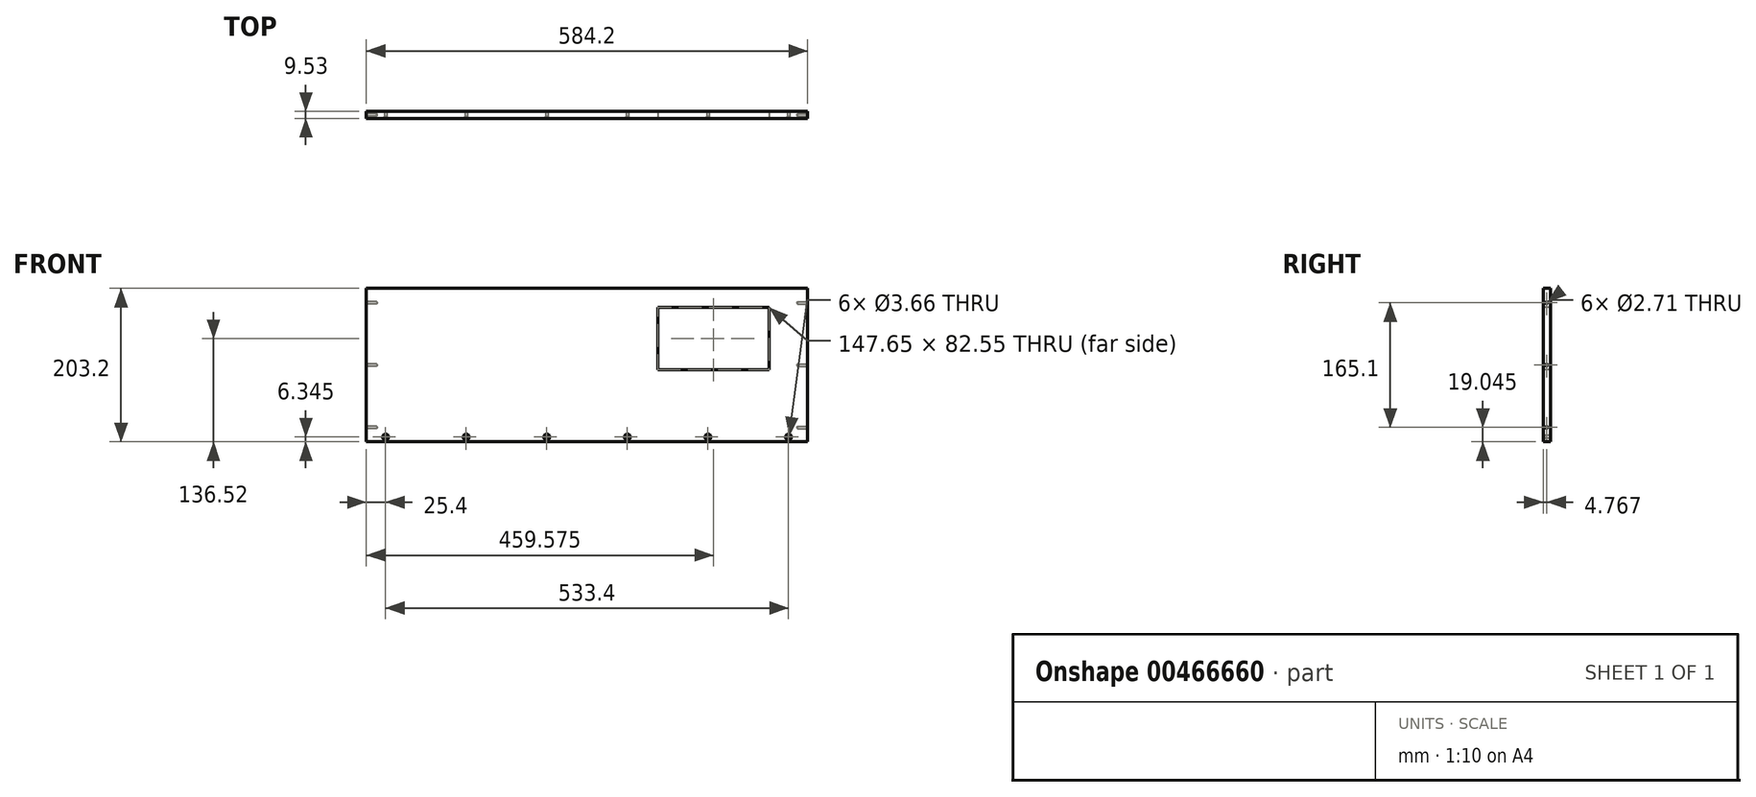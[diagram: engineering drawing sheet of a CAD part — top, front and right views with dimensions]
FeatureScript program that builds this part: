
annotation { "Feature Type Name" : "Feature", "Feature Type Description" : "" }
export const myFeature = defineFeature(function(context is Context, id is Id, definition is map)
    precondition{}
    {
        {
            var Q0;
            Q0=qCreatedBy(makeId("Front.planeOp"),FACE);
            var sketch = newSketch(context, id + "F0", { "sketchPlane" : qUnion([Q0])});
            skLineSegment(sketch, "E0.bottom", {"start": v(0, -14.34) * mm, "end": v(-584.2, -14.34) * mm});
            skLineSegment(sketch, "E0.top", {"start": v(0, 188.86) * mm, "end": v(-584.2, 188.86) * mm});
            skLineSegment(sketch, "E0.left", {"start": v(0, -14.34) * mm, "end": v(0, 188.86) * mm});
            skLineSegment(sketch, "E0.right", {"start": v(-584.2, -14.34) * mm, "end": v(-584.2, 188.86) * mm});
            skSolve(sketch);
        }
        {
            var Q0;
            Q0 = qSketchRegion(id + "F0", true);
            extrude(context, id + "F1", {"entities" : qUnion([Q0]), "depth" : 9.52 * mm});
        }
        {
            var Q0;
            Q0=makeQuery(id+"F1.opExtrude","CAP_FACE",FACE,{"disambiguationData":[OSD([sQuery(id+"F0.wireOp",EDGE,"E0.bottom"),sQuery(id+"F0.wireOp",EDGE,"E0.top"),sQuery(id+"F0.wireOp",EDGE,"E0.left"),sQuery(id+"F0.wireOp",EDGE,"E0.right")])],"isStart":false});
            var sketch = newSketch(context, id + "F2", { "sketchPlane" : qUnion([Q0])});
            skPoint(sketch, "E1", {"position": v(-25.4, -8) * mm});
            skPoint(sketch, "E2.1.0.0", {"position": v(-132.08, -8) * mm});
            skPoint(sketch, "E2.2.0.0", {"position": v(-238.76, -8) * mm});
            skPoint(sketch, "E2.3.0.0", {"position": v(-345.44, -8) * mm});
            skPoint(sketch, "E2.4.0.0", {"position": v(-452.12, -8) * mm});
            skPoint(sketch, "E2.5.0.0", {"position": v(-558.8, -8) * mm});
            skLineSegment(sketch, "E2.direction1", {"start": v(-25.4, -8) * mm, "end": v(-132.08, -8) * mm, "construction": true});
            skSolve(sketch);
        }
        {
            var Q0;
            Q0=sQuery(id+"F2.wireOp",VERTEX,"E2.5.0.0");
            var Q1;
            Q1=sQuery(id+"F2.wireOp",VERTEX,"E2.3.0.0");
            var Q2;
            Q2=sQuery(id+"F2.wireOp",VERTEX,"f863c8bc-1770-4883-823e-4a9a9a39e688.0.1.0");
            var Q3;
            Q3=sQuery(id+"F2.wireOp",VERTEX,"E2.4.0.0");
            var Q4;
            Q4=sQuery(id+"F2.wireOp",VERTEX,"E2.2.0.0");
            var Q5;
            Q5=sQuery(id+"F2.wireOp",VERTEX,"f863c8bc-1770-4883-823e-4a9a9a39e688.0.2.0");
            var Q6;
            Q6=sQuery(id+"F2.wireOp",VERTEX,"E2.1.0.0");
            var Q7;
            Q7=sQuery(id+"F2.wireOp",VERTEX,"87545330-7da3-4d45-876c-430507ea1bf7.0.1.0");
            var Q8;
            Q8=sQuery(id+"F2.wireOp",VERTEX,"87545330-7da3-4d45-876c-430507ea1bf7.0.2.0");
            var Q9;
            Q9=sQuery(id+"F2.wireOp",VERTEX,"eef8172f-6746-48e1-8af2-2bb0cf11cfa1");
            var Q10;
            Q10=sQuery(id+"F2.wireOp",VERTEX,"0cc6952c-0d8d-488b-9108-ef1e5a8eb671");
            var Q11;
            Q11=sQuery(id+"F2.wireOp",VERTEX,"E1");
            var Q12;
            Q12=makeQuery(id+"F1.opExtrude","SWEPT_BODY",BODY,{"disambiguationData":[OSD([sQuery(id+"F0.wireOp",EDGE,"E0.bottom"),sQuery(id+"F0.wireOp",EDGE,"E0.top"),sQuery(id+"F0.wireOp",EDGE,"E0.left"),sQuery(id+"F0.wireOp",EDGE,"E0.right")])]});
            hole(context, id + "F3", {"style" : HoleStyle.C_SINK, "endStyle" : HoleEndStyle.BLIND, "standardTappedOrClearance" : lookupTablePath({ "standard" : "ANSI", "fit" : "Close", "size" : "#6", "type" : "Clearance" }), "standardBlindInLast" : lookupTablePath({ "fit" : "Close", "standard" : "ANSI", "size" : "#6", "type" : "Clearance" }), "holeDiameter" : 3.66 * mm, "cSinkDiameter" : 7.8 * mm, "cSinkAngle" : 82 * degree, "holeDepth" : 10.3 * mm, "isTappedThrough" : true, "tappedDepth" : 6.34 * mm, "tapClearance" : 5, "locations" : qUnion([Q0, Q1, Q2, Q3, Q4, Q5, Q6, Q7, Q8, Q9, Q10, Q11]), "scope" : qUnion([Q12])});
        }
        {
            var Q0;
            Q0=makeQuery(id+"F1.opExtrude","CAP_FACE",FACE,{"disambiguationData":[OSD([sQuery(id+"F0.wireOp",EDGE,"E0.bottom"),sQuery(id+"F0.wireOp",EDGE,"E0.top"),sQuery(id+"F0.wireOp",EDGE,"E0.left"),sQuery(id+"F0.wireOp",EDGE,"E0.right")])],"isStart":false});
            var sketch = newSketch(context, id + "F4", { "sketchPlane" : qUnion([Q0])});
            skLineSegment(sketch, "E3.bottom", {"start": v(-198.45, 163.46) * mm, "end": v(-50.8, 163.46) * mm});
            skLineSegment(sketch, "E3.top", {"start": v(-198.45, 80.9) * mm, "end": v(-50.8, 80.9) * mm});
            skLineSegment(sketch, "E3.left", {"start": v(-198.45, 163.46) * mm, "end": v(-198.45, 80.9) * mm});
            skLineSegment(sketch, "E3.right", {"start": v(-50.8, 163.46) * mm, "end": v(-50.8, 80.9) * mm});
            skSolve(sketch);
        }
        {
            var Q0;
            Q0 = qSketchRegion(id + "F4", true);
            extrude(context, id + "F5", {"entities" : qUnion([Q0]), "operationType" : NewBodyOperationType.REMOVE, "endBound" : BoundingType.THROUGH_ALL, "oppositeDirection" : true, "depth" : 25.4 * mm});
        }
        {
            var Q0;
            Q0=makeQuery(id+"F1.opExtrude","SWEPT_FACE",FACE,{"disambiguationData":[OSD([sQuery(id+"F0.wireOp",EDGE,"E0.right")])]});
            var sketch = newSketch(context, id + "F6", { "sketchPlane" : qUnion([Q0])});
            skPoint(sketch, "E4", {"position": v(4.76, 4.7) * mm});
            skPoint(sketch, "E5.0.1.0", {"position": v(4.76, 87.26) * mm});
            skPoint(sketch, "E5.0.2.0", {"position": v(4.76, 169.8) * mm});
            skLineSegment(sketch, "E5.direction1", {"start": v(4.76, 4.7) * mm, "end": v(30.16, 4.7) * mm, "construction": true});
            skLineSegment(sketch, "E5.direction2", {"start": v(4.76, 4.7) * mm, "end": v(4.76, 87.26) * mm, "construction": true});
            skSolve(sketch);
        }
        {
            var Q0;
            Q0=sQuery(id+"F6.wireOp",VERTEX,"E5.0.2.0");
            var Q1;
            Q1=sQuery(id+"F6.wireOp",VERTEX,"E5.0.1.0");
            var Q2;
            Q2=sQuery(id+"F6.wireOp",VERTEX,"E4");
            var Q3;
            Q3=makeQuery(id+"F1.opExtrude","SWEPT_BODY",BODY,{"disambiguationData":[OSD([sQuery(id+"F0.wireOp",EDGE,"E0.bottom"),sQuery(id+"F0.wireOp",EDGE,"E0.top"),sQuery(id+"F0.wireOp",EDGE,"E0.left"),sQuery(id+"F0.wireOp",EDGE,"E0.right")])]});
            hole(context, id + "F7", {"style" : HoleStyle.SIMPLE, "endStyle" : HoleEndStyle.BLIND, "standardTappedOrClearance" : lookupTablePath({ "standard" : "ANSI", "engagement" : "75%", "pitch" : "32 tpi", "size" : "#6", "type" : "Tapped" }), "standardBlindInLast" : lookupTablePath({ "standard" : "ANSI", "engagement" : "75%", "pitch" : "32 tpi", "size" : "#6", "type" : "Tapped" }), "holeDiameter" : 2.7 * mm, "showTappedDepth" : true, "holeDepth" : 13.5 * mm, "isTappedThrough" : true, "tappedDepth" : 9.52 * mm, "tapClearance" : 5, "locations" : qUnion([Q0, Q1, Q2]), "scope" : qUnion([Q3]), "majorDiameter" : 3.5 * mm});
        }
        {
            var Q0;
            Q0=makeQuery(id+"F1.opExtrude","SWEPT_FACE",FACE,{"disambiguationData":[OSD([sQuery(id+"F0.wireOp",EDGE,"E0.left")])]});
            var sketch = newSketch(context, id + "F8", { "sketchPlane" : qUnion([Q0])});
            skPoint(sketch, "E6", {"position": v(-4.76, 4.7) * mm});
            skPoint(sketch, "E7.0.1.0", {"position": v(-4.76, 87.26) * mm});
            skPoint(sketch, "E7.0.2.0", {"position": v(-4.76, 169.8) * mm});
            skLineSegment(sketch, "E7.direction1", {"start": v(-4.76, 4.7) * mm, "end": v(20.64, 4.7) * mm, "construction": true});
            skLineSegment(sketch, "E7.direction2", {"start": v(-4.76, 4.7) * mm, "end": v(-4.76, 87.26) * mm, "construction": true});
            skSolve(sketch);
        }
        {
            var Q0;
            Q0=sQuery(id+"F8.wireOp",VERTEX,"E6");
            var Q1;
            Q1=sQuery(id+"F8.wireOp",VERTEX,"E7.0.1.0");
            var Q2;
            Q2=sQuery(id+"F8.wireOp",VERTEX,"E7.0.2.0");
            var Q3;
            Q3=makeQuery(id+"F1.opExtrude","SWEPT_BODY",BODY,{"disambiguationData":[OSD([sQuery(id+"F0.wireOp",EDGE,"E0.bottom"),sQuery(id+"F0.wireOp",EDGE,"E0.top"),sQuery(id+"F0.wireOp",EDGE,"E0.left"),sQuery(id+"F0.wireOp",EDGE,"E0.right")])]});
            hole(context, id + "F9", {"style" : HoleStyle.SIMPLE, "endStyle" : HoleEndStyle.BLIND, "standardTappedOrClearance" : lookupTablePath({ "standard" : "ANSI", "engagement" : "75%", "pitch" : "32 tpi", "size" : "#6", "type" : "Tapped" }), "standardBlindInLast" : lookupTablePath({ "standard" : "ANSI", "engagement" : "75%", "pitch" : "32 tpi", "size" : "#6", "type" : "Tapped" }), "holeDiameter" : 2.7 * mm, "showTappedDepth" : true, "holeDepth" : 13.5 * mm, "isTappedThrough" : true, "tappedDepth" : 9.52 * mm, "tapClearance" : 5, "locations" : qUnion([Q0, Q1, Q2]), "scope" : qUnion([Q3]), "majorDiameter" : 3.5 * mm});
        }
    });
